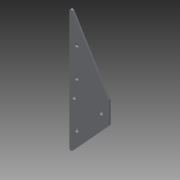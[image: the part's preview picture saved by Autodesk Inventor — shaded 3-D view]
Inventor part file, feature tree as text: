
AUTODESK INVENTOR PART (.ipt)
format: ipt  version: 2013 (Build 170138000, 138)  size: 122,368 bytes
history: native  units: in
note: dims shown in document units (in); Inventor stores cm internally (conversion verified against a paired STEP export)
features: extrude x5, sketch x5, fillet x3
ambient origin geometry x8: Origin, YZ Plane, XZ Plane, XY Plane, X Axis, Y Axis, Z Axis, Center Point
bodies: Solid1 (feature_tree)
feature tree (13):
  extrude  "Extrusion1"  Depth=6.0in
  extrude  "Extrusion2"  Depth=0.28in
  fillet  "Fillet1"  Radius=0.28in
  extrude  "Extrusion3"  Depth=0.5in
  fillet  "Fillet2"  Radius=0.56in
  fillet  "Fillet3"  Radius=0.31in
  extrude  "Extrusion4"  Depth=0.125in
  extrude  "Extrusion5"  Depth=0.266in
  sketch  "Sketch1"  dims[d1=1.5in d2=6.0in]
  sketch  "Sketch2"  dims[d3=0.125in d4=0.0in d5=0.28in d6=0.28in]
  sketch  "Sketch3"  dims[d7=0.5in d8=0.5in d9=0.56in d11=0.31in]
  sketch  "Sketch4"  dims[d12=1.0in d13=0.0in d14=0.125in]
  sketch  "Sketch5"  dims[d15=0.266in d16=0.266in d17=0.5in d18=0.5in d19=1.737in d20=2.0in d21=1.0in d22=0.0in d23=0.125in d24=3.0in d25=2.75in d26=2.75in d27=0.125in d28=0.266in d29=3.125in d30=0.5in d31=1.0in d32=0.0in d33=1.0in d34=0.0in]
